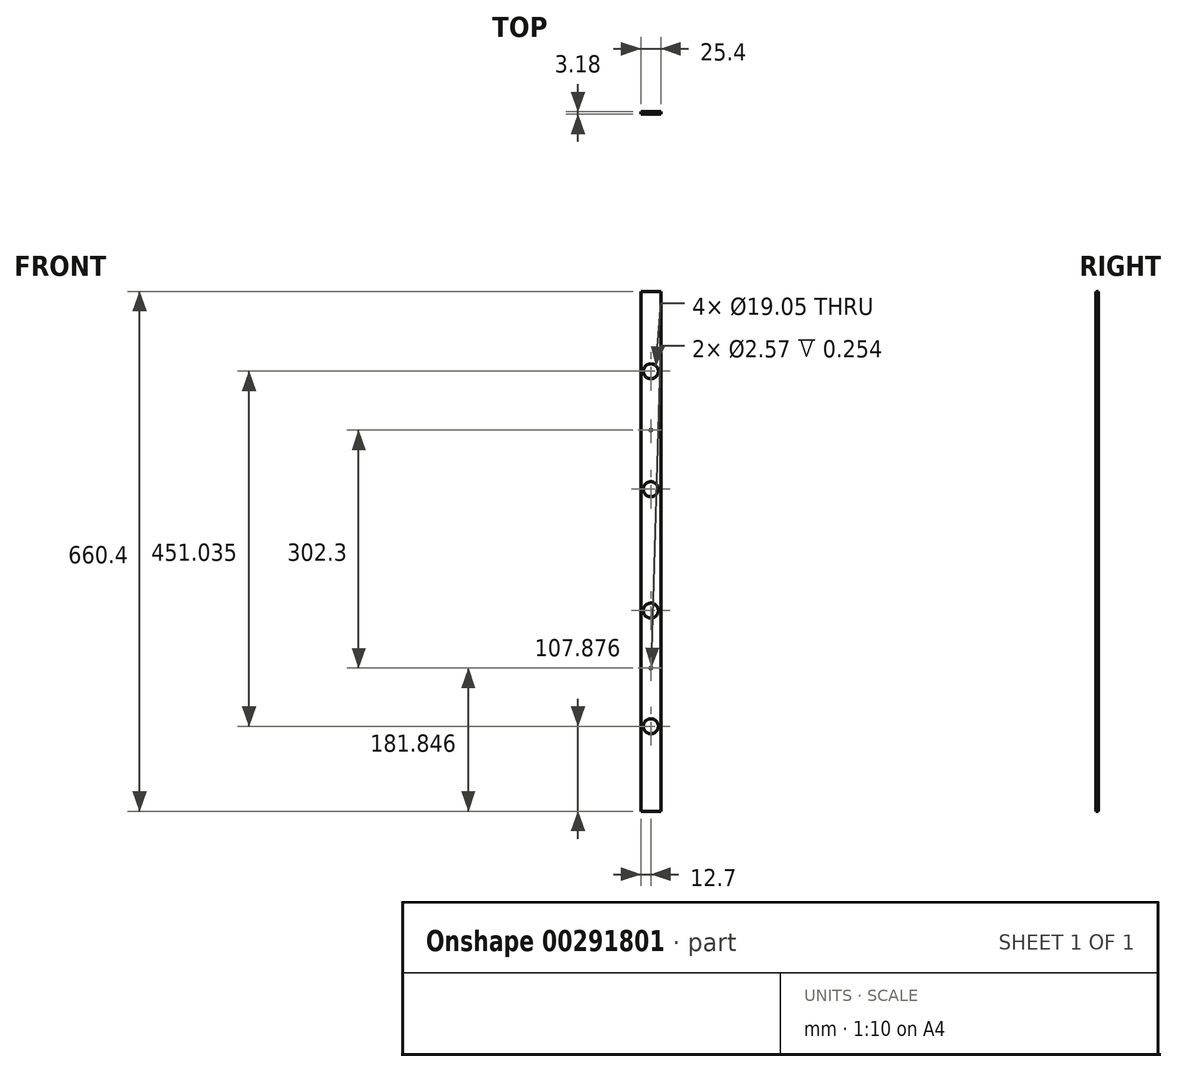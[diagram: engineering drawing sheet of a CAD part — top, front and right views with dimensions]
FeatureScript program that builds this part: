
annotation { "Feature Type Name" : "Feature", "Feature Type Description" : "" }
export const myFeature = defineFeature(function(context is Context, id is Id, definition is map)
    precondition{}
    {
        {
            var Q0;
            Q0=qCreatedBy(makeId("Front.planeOp"),FACE);
            var sketch = newSketch(context, id + "F0", { "sketchPlane" : qUnion([Q0])});
            skLineSegment(sketch, "E0.bottom", {"start": v(12.7, 330.2) * mm, "end": v(-12.7, 330.2) * mm});
            skLineSegment(sketch, "E0.top", {"start": v(12.7, -330.2) * mm, "end": v(-12.7, -330.2) * mm});
            skLineSegment(sketch, "E0.left", {"start": v(12.7, 330.2) * mm, "end": v(12.7, -330.2) * mm});
            skLineSegment(sketch, "E0.right", {"start": v(-12.7, 330.2) * mm, "end": v(-12.7, -330.2) * mm});
            skPoint(sketch, "E0.middle", {"position": v(0, 0) * mm});
            skSolve(sketch);
        }
        {
            var Q0;
            Q0 = qSketchRegion(id + "F0", true);
            extrude(context, id + "F1", {"entities" : qUnion([Q0]), "depth" : 3.17 * mm});
        }
        {
            var Q0;
            Q0=makeQuery(id+"F1.opExtrude","CAP_FACE",FACE,{"disambiguationData":[OSD([sQuery(id+"F0.wireOp",EDGE,"E0.bottom"),sQuery(id+"F0.wireOp",EDGE,"E0.top"),sQuery(id+"F0.wireOp",EDGE,"E0.left"),sQuery(id+"F0.wireOp",EDGE,"E0.right")])],"isStart":false});
            var sketch = newSketch(context, id + "F2", { "sketchPlane" : qUnion([Q0])});
            skCircle(sketch, "E1", {"center": v(0, 78.92) * mm, "radius": 9.52 * mm});
            skSolve(sketch);
        }
        {
            var Q0;
            Q0 = qSketchRegion(id + "F2", true);
            extrude(context, id + "F3", {"entities" : qUnion([Q0]), "operationType" : NewBodyOperationType.REMOVE, "oppositeDirection" : true, "depth" : 25.4 * mm});
        }
        {
            var Q0;
            Q0=makeQuery(id+"F1.opExtrude","CAP_FACE",FACE,{"disambiguationData":[OSD([sQuery(id+"F0.wireOp",EDGE,"E0.bottom"),sQuery(id+"F0.wireOp",EDGE,"E0.top"),sQuery(id+"F0.wireOp",EDGE,"E0.left"),sQuery(id+"F0.wireOp",EDGE,"E0.right")])],"isStart":false});
            var sketch = newSketch(context, id + "F4", { "sketchPlane" : qUnion([Q0])});
            skCircle(sketch, "E2", {"center": v(0, -75.35) * mm, "radius": 9.53 * mm});
            skSolve(sketch);
        }
        {
            var Q0;
            Q0 = qSketchRegion(id + "F4", true);
            extrude(context, id + "F5", {"entities" : qUnion([Q0]), "operationType" : NewBodyOperationType.REMOVE, "oppositeDirection" : true, "depth" : 25.4 * mm});
        }
        {
            var Q0;
            Q0=makeQuery(id+"F1.opExtrude","CAP_FACE",FACE,{"disambiguationData":[OSD([sQuery(id+"F0.wireOp",EDGE,"E0.bottom"),sQuery(id+"F0.wireOp",EDGE,"E0.top"),sQuery(id+"F0.wireOp",EDGE,"E0.left"),sQuery(id+"F0.wireOp",EDGE,"E0.right")])],"isStart":false});
            var sketch = newSketch(context, id + "F6", { "sketchPlane" : qUnion([Q0])});
            skCircle(sketch, "E3", {"center": v(0, -222.32) * mm, "radius": 9.53 * mm});
            skSolve(sketch);
        }
        {
            var Q0;
            Q0 = qSketchRegion(id + "F6", true);
            extrude(context, id + "F7", {"entities" : qUnion([Q0]), "operationType" : NewBodyOperationType.REMOVE, "oppositeDirection" : true, "depth" : 25.4 * mm});
        }
        {
            var Q0;
            Q0=makeQuery(id+"F1.opExtrude","CAP_FACE",FACE,{"disambiguationData":[OSD([sQuery(id+"F0.wireOp",EDGE,"E0.bottom"),sQuery(id+"F0.wireOp",EDGE,"E0.top"),sQuery(id+"F0.wireOp",EDGE,"E0.left"),sQuery(id+"F0.wireOp",EDGE,"E0.right")])],"isStart":true});
            var sketch = newSketch(context, id + "F8", { "sketchPlane" : qUnion([Q0])});
            skCircle(sketch, "E4", {"center": v(0, 228.71) * mm, "radius": 9.53 * mm});
            skSolve(sketch);
        }
        {
            var Q0;
            Q0 = qSketchRegion(id + "F8", true);
            extrude(context, id + "F9", {"entities" : qUnion([Q0]), "operationType" : NewBodyOperationType.REMOVE, "oppositeDirection" : true, "depth" : 25.4 * mm});
        }
        {
            var Q0;
            Q0=makeQuery(id+"F1.opExtrude","CAP_FACE",FACE,{"disambiguationData":[OSD([sQuery(id+"F0.wireOp",EDGE,"E0.bottom"),sQuery(id+"F0.wireOp",EDGE,"E0.top"),sQuery(id+"F0.wireOp",EDGE,"E0.left"),sQuery(id+"F0.wireOp",EDGE,"E0.right")])],"isStart":false});
            var sketch = newSketch(context, id + "F10", { "sketchPlane" : qUnion([Q0])});
            skLineSegment(sketch, "E5", {"start": v(0, 219.19) * mm, "end": v(0, 153.86) * mm});
            skSolve(sketch);
        }
        {
            var Q0;
            {var subQ3=sQuery(id+"F0.wireOp",EDGE,"E0.bottom");Q0=makeQuery(id+"F10.imprint","IMPRINT",FACE,{"disambiguationData":[TD([[makeQuery(id+"F10.imprint","IMPRINT",EDGE,{"derivedFrom":makeQuery(id+"F1.opExtrude","CAP_EDGE",EDGE,{"disambiguationData":[OSD([subQ3])],"isStart":false})}),1.0]])]});}
            var sketch = newSketch(context, id + "F11", { "sketchPlane" : qUnion([Q0])});
            skCircle(sketch, "E6", {"center": v(0, 153.95) * mm, "radius": 1.29 * mm});
            skSolve(sketch);
        }
        {
            var Q0;
            Q0 = qSketchRegion(id + "F11", true);
            extrude(context, id + "F12", {"entities" : qUnion([Q0]), "operationType" : NewBodyOperationType.REMOVE, "oppositeDirection" : true, "depth" : 0.25 * mm});
        }
        {
            var Q0;
            {var subQ3=sQuery(id+"F0.wireOp",EDGE,"E0.bottom");Q0=makeQuery(id+"F10.imprint","IMPRINT",FACE,{"disambiguationData":[TD([[makeQuery(id+"F10.imprint","IMPRINT",EDGE,{"derivedFrom":makeQuery(id+"F1.opExtrude","CAP_EDGE",EDGE,{"disambiguationData":[OSD([subQ3])],"isStart":false})}),1.0]])]});}
            var sketch = newSketch(context, id + "F13", { "sketchPlane" : qUnion([Q0])});
            skCircle(sketch, "E7", {"center": v(0, -148.35) * mm, "radius": 1.28 * mm});
            skSolve(sketch);
        }
        {
            var Q0;
            Q0 = qSketchRegion(id + "F13", true);
            extrude(context, id + "F14", {"entities" : qUnion([Q0]), "operationType" : NewBodyOperationType.REMOVE, "oppositeDirection" : true, "depth" : 0.25 * mm});
        }
    });
